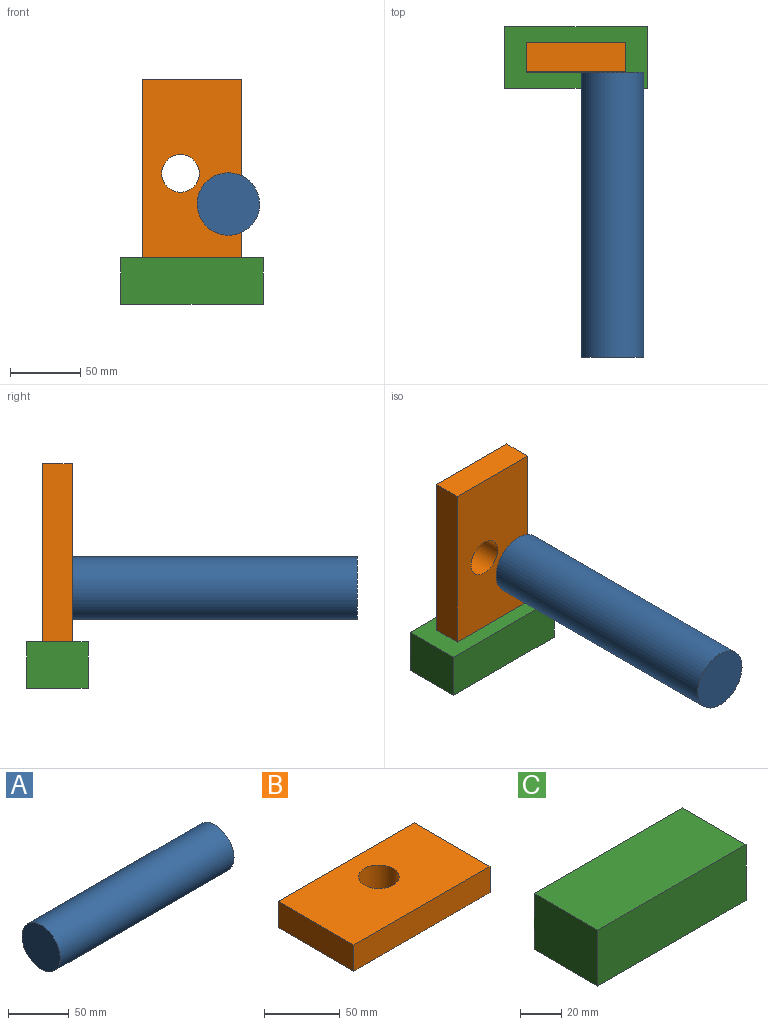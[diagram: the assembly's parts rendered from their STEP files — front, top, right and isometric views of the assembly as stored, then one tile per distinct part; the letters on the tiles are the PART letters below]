
ASSEMBLY  parts=3 mates=2
PART A: 3 faces, bbox 203.2x44.6x44.6 mm
  f0: cylinder r=22.31mm len=203.2mm, axis (-1,0,0), area 28482.2mm2, adj f1,f2
  f1: plane 44.62x44.62mm, normal (1,0,0), area 1563.5mm2, adj f0
  f2: plane 44.62x44.62mm, normal (-1,0,0), area 1563.5mm2, adj f0
PART B: 7 faces, bbox 127x70.8x21.1 mm
  f0: plane 127x70.82mm, normal (0,0,1), area 8430.6mm2, adj f1,f3,f4,f5,f6
  f1: plane 127x21.1mm, normal (0,-1,0), area 2679.1mm2, adj f0,f2,f4,f5
  f2: plane 127x70.82mm, normal (0,0,-1), area 8430.6mm2, adj f1,f3,f4,f5,f6
  f3: plane 127x21.1mm, normal (0,1,0), area 2679.1mm2, adj f0,f2,f4,f5
  f4: plane 70.82x21.1mm, normal (1,0,0), area 1493.9mm2, adj f0,f1,f2,f3
  f5: plane 70.82x21.1mm, normal (-1,0,0), area 1493.9mm2, adj f0,f1,f2,f3
  f6: cylinder r=13.39mm len=26.78mm, axis (0,0,1), area 1775mm2, adj f0,f2
PART C: 6 faces, bbox 101.6x43.7x33.1 mm
  f0: plane 101.6x43.7mm, normal (0,0,1), area 4439.6mm2, adj f1,f3,f4,f5
  f1: plane 101.6x33.15mm, normal (0,-1,0), area 3368mm2, adj f0,f2,f4,f5
  f2: plane 101.6x43.7mm, normal (0,0,-1), area 4439.6mm2, adj f1,f3,f4,f5
  f3: plane 101.6x33.15mm, normal (0,1,0), area 3368mm2, adj f0,f2,f4,f5
  f4: plane 43.7x33.15mm, normal (1,0,0), area 1448.5mm2, adj f0,f1,f2,f3
  f5: plane 43.7x33.15mm, normal (-1,0,0), area 1448.5mm2, adj f0,f1,f2,f3
PLACE A rot(axis=(0.71,0.71,0),180deg) t=(200.16,-86.61,75.71)mm
PLACE B rot(axis=(-0.58,0.58,0.58),120deg) t=(239.16,106.34,153.24)mm
PLACE C rot(axis=(1,0,0),180deg) t=(189.56,92.18,45.52)mm
MATE fastened A.f0 <-> B.f2  axis (0,1,0) through (266.31,116.59,64.56)mm
MATE fastened B.f4 <-> C.f2  axis (0,0,-1) through (240.36,127.13,26.24)mm
